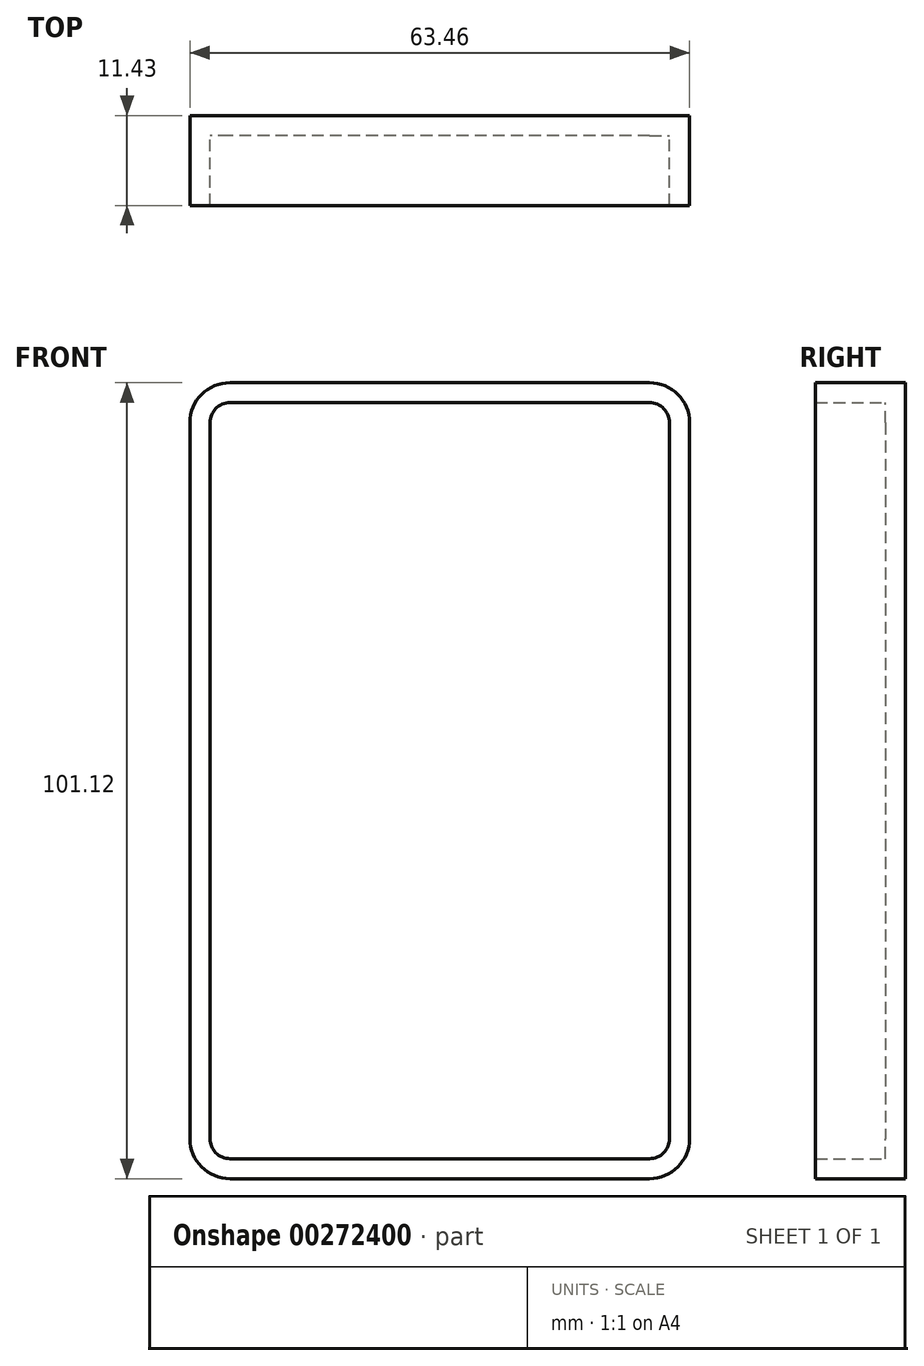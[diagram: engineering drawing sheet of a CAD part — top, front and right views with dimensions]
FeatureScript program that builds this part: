
annotation { "Feature Type Name" : "Feature", "Feature Type Description" : "" }
export const myFeature = defineFeature(function(context is Context, id is Id, definition is map)
    precondition{}
    {
        {
            var Q0;
            Q0=qCreatedBy(makeId("Front.planeOp"),FACE);
            var sketch = newSketch(context, id + "F0", { "sketchPlane" : qUnion([Q0])});
            skLineSegment(sketch, "E0.bottom", {"start": v(-68.93, 32.85) * mm, "end": v(-132.4, 32.85) * mm});
            skLineSegment(sketch, "E0.top", {"start": v(-68.93, -68.27) * mm, "end": v(-132.4, -68.27) * mm});
            skLineSegment(sketch, "E0.left", {"start": v(-68.93, 32.85) * mm, "end": v(-68.93, -68.27) * mm});
            skLineSegment(sketch, "E0.right", {"start": v(-132.4, 32.85) * mm, "end": v(-132.4, -68.27) * mm});
            skSolve(sketch);
        }
        {
            var Q0;
            Q0=makeQuery(id+"F0.imprint","IMPRINT",FACE,{"disambiguationData":[TD([[makeQuery(id+"F0.imprint","IMPRINT",EDGE,{"derivedFrom":sQuery(id+"F0.wireOp",EDGE,"E0.bottom")}),1.0]])]});
            extrude(context, id + "F1", {"entities" : qUnion([Q0]), "depth" : 11.43 * mm});
        }
        {
            var Q0;
            Q0=makeQuery(id+"F1.opExtrude","SWEPT_EDGE",EDGE,{"disambiguationData":[OSD([sQuery(id+"F0.wireOp",EDGE,"E0.bottom"),sQuery(id+"F0.wireOp",EDGE,"E0.left")])]});
            var Q1;
            Q1=makeQuery(id+"F1.opExtrude","SWEPT_EDGE",EDGE,{"disambiguationData":[OSD([sQuery(id+"F0.wireOp",EDGE,"E0.bottom"),sQuery(id+"F0.wireOp",EDGE,"E0.right")])]});
            var Q2;
            Q2=makeQuery(id+"F1.opExtrude","SWEPT_EDGE",EDGE,{"disambiguationData":[OSD([sQuery(id+"F0.wireOp",EDGE,"E0.top"),sQuery(id+"F0.wireOp",EDGE,"E0.left")])]});
            var Q3;
            Q3=makeQuery(id+"F1.opExtrude","SWEPT_EDGE",EDGE,{"disambiguationData":[OSD([sQuery(id+"F0.wireOp",EDGE,"E0.top"),sQuery(id+"F0.wireOp",EDGE,"E0.right")])]});
            fillet(context, id + "F2", {"entities" : qUnion([Q0, Q1, Q2, Q3]), "radius" : 5.08 * mm, "tangentPropagation" : true, "allowEdgeOverflow" : false});
        }
        {
            var Q0;
            Q0=makeQuery(id+"F1.opExtrude","CAP_FACE",FACE,{"disambiguationData":[OSD([sQuery(id+"F0.wireOp",EDGE,"E0.bottom"),sQuery(id+"F0.wireOp",EDGE,"E0.top"),sQuery(id+"F0.wireOp",EDGE,"E0.left"),sQuery(id+"F0.wireOp",EDGE,"E0.right")])],"isStart":false});
            shell(context, id + "F3", {"entities" : qUnion([Q0]), "thickness" : 2.54 * mm});
        }
    });
